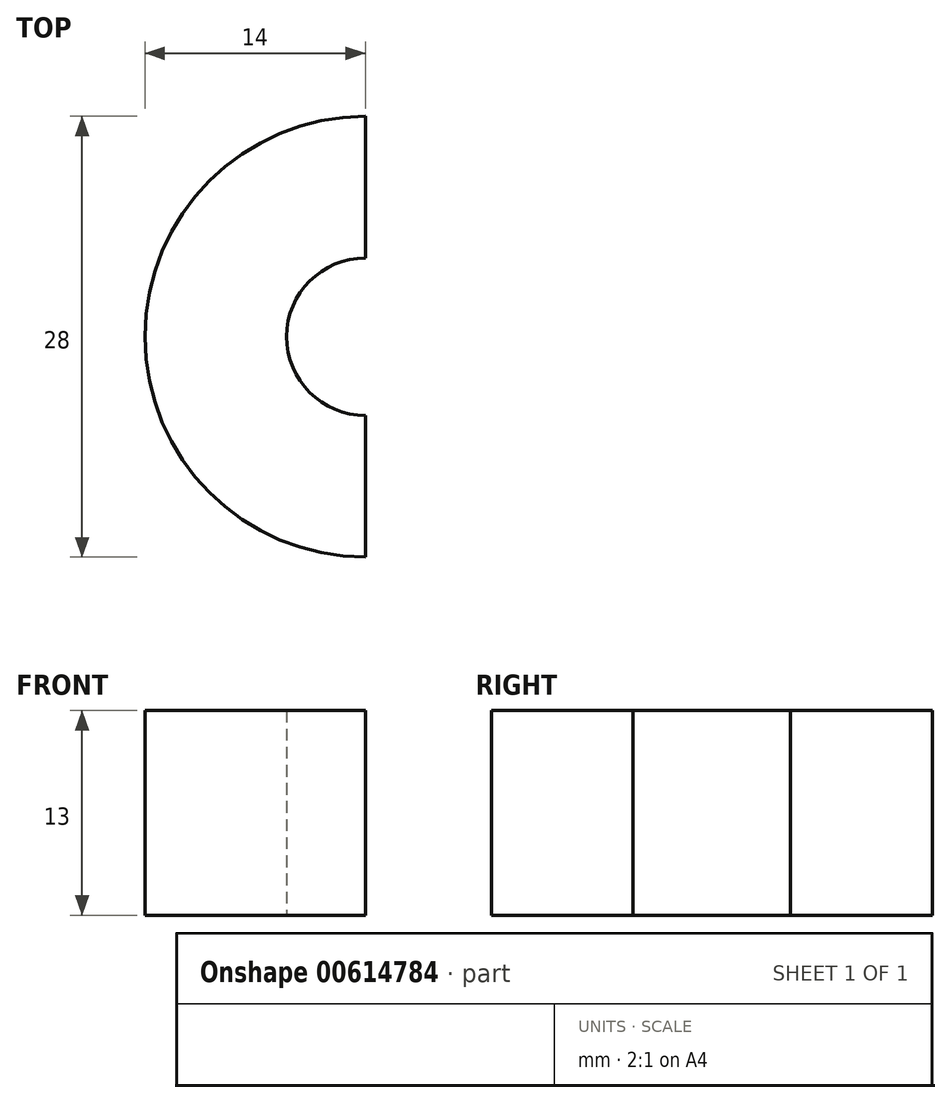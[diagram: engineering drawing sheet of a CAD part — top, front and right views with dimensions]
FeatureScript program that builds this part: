
annotation { "Feature Type Name" : "Feature", "Feature Type Description" : "" }
export const myFeature = defineFeature(function(context is Context, id is Id, definition is map)
    precondition{}
    {
        {
            var Q0;
            Q0=qCreatedBy(makeId("Top.planeOp"),FACE);
            var sketch = newSketch(context, id + "F0", { "sketchPlane" : qUnion([Q0])});
            skArc(sketch, "E0", {"start": v(0, 14) * mm, "mid": v(-14, 0) * mm, "end": v(0, -14) * mm});
            skArc(sketch, "E1", {"start": v(0, 5) * mm, "mid": v(-5, 0) * mm, "end": v(0, -5) * mm});
            skLineSegment(sketch, "E2", {"start": v(0, 14) * mm, "end": v(0, 5) * mm});
            skLineSegment(sketch, "E3", {"start": v(0, -5) * mm, "end": v(0, -14) * mm});
            skSolve(sketch);
        }
        {
            var Q0;
            Q0=makeQuery(id+"F0.imprint","IMPRINT",FACE,{"disambiguationData":[TD([[makeQuery(id+"F0.imprint","IMPRINT",EDGE,{"derivedFrom":sQuery(id+"F0.wireOp",EDGE,"E0")}),1.0]])]});
            extrude(context, id + "F1", {"entities" : qUnion([Q0]), "depth" : 13 * mm, "offsetDistance" : 25 * mm});
        }
    });
